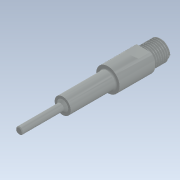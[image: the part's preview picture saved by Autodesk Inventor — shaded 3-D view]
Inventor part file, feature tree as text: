
AUTODESK INVENTOR PART (.ipt)
format: ipt  version: 2021 (Build 250183000, 183)  size: 235,008 bytes
history: native  units: mm
features: other x1, thread x1
ambient origin geometry x8: Origin, YZ Plane, XZ Plane, XY Plane, X Axis, Y Axis, Z Axis, Center Point
bodies: Body1 (feature_tree)
feature tree (2):
  other  "Sólido1"
  thread  "Rosca1"  [1 undecoded]
note: 1 required parameter value undecoded (feature->parameter linkage not recoverable at this tier; creation-order binding heuristic only, values carry confidence <= 0.55)
